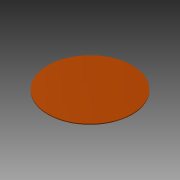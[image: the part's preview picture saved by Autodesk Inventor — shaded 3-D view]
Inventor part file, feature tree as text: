
AUTODESK INVENTOR PART (.ipt)
format: ipt  version: 2013 (Build 170138000, 138)  size: 67,072 bytes
history: native  units: mm
features: extrude x1, sketch x1
ambient origin geometry x8: Origin, YZ Plane, XZ Plane, XY Plane, X Axis, Y Axis, Z Axis, Center Point
bodies: Solid1 (feature_tree)
feature tree (2):
  extrude  "Extrusion1"  Depth=2.0mm TaperAngle=0.0deg
  sketch  "Sketch1"  dims[d0=200.0mm d2=2.0mm d3=0.0mm]
